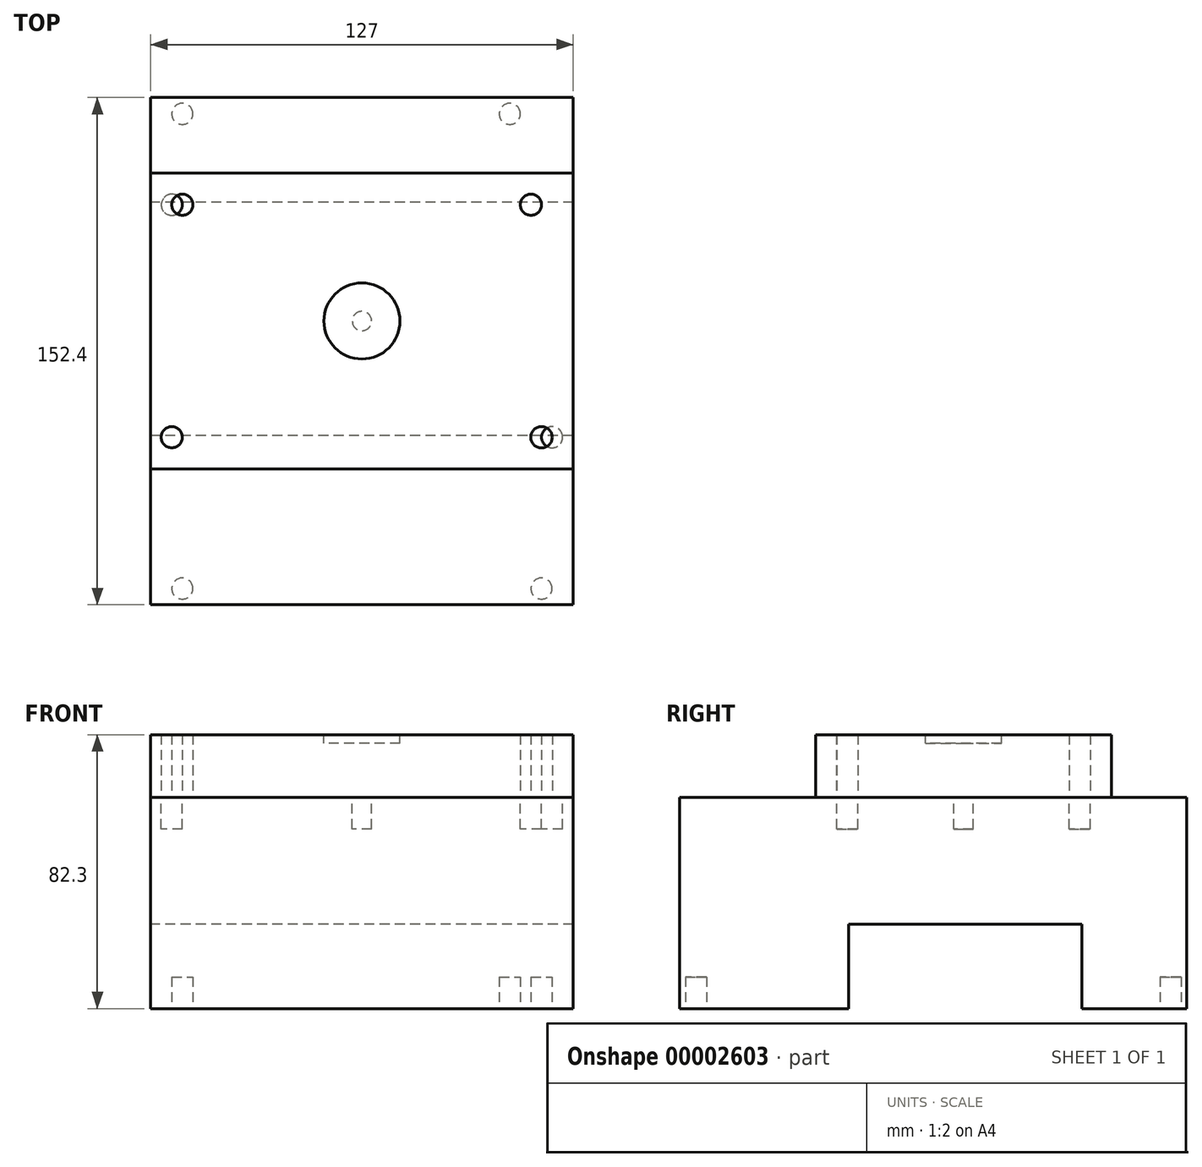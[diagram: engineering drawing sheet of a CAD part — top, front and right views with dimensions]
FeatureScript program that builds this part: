
annotation { "Feature Type Name" : "Feature", "Feature Type Description" : "" }
export const myFeature = defineFeature(function(context is Context, id is Id, definition is map)
    precondition{}
    {
        {
            var Q0;
            Q0=qCreatedBy(makeId("Top.planeOp"),FACE);
            var sketch = newSketch(context, id + "F0", { "sketchPlane" : qUnion([Q0])});
            skLineSegment(sketch, "E0.bottom", {"start": v(0, 0) * mm, "end": v(127, 0) * mm});
            skLineSegment(sketch, "E0.top", {"start": v(0, 152.4) * mm, "end": v(127, 152.4) * mm});
            skLineSegment(sketch, "E0.left", {"start": v(0, 0) * mm, "end": v(0, 152.4) * mm});
            skLineSegment(sketch, "E0.right", {"start": v(127, 0) * mm, "end": v(127, 152.4) * mm});
            skSolve(sketch);
        }
        {
            var Q0;
            Q0 = qSketchRegion(id + "F0", true);
            extrude(context, id + "F1", {"entities" : qUnion([Q0]), "depth" : 63.5 * mm});
        }
        {
            var Q0;
            Q0=makeQuery(id+"F1.opExtrude","CAP_FACE",FACE,{"disambiguationData":[OSD([sQuery(id+"F0.wireOp",EDGE,"E0.bottom"),sQuery(id+"F0.wireOp",EDGE,"E0.top"),sQuery(id+"F0.wireOp",EDGE,"E0.left"),sQuery(id+"F0.wireOp",EDGE,"E0.right")])],"isStart":true});
            var sketch = newSketch(context, id + "F2", { "sketchPlane" : qUnion([Q0])});
            skCircle(sketch, "E1", {"center": v(107.95, -147.51) * mm, "radius": 3.18 * mm});
            skCircle(sketch, "E2", {"center": v(9.52, -147.51) * mm, "radius": 3.18 * mm});
            skCircle(sketch, "E3", {"center": v(9.52, -4.89) * mm, "radius": 3.18 * mm});
            skCircle(sketch, "E4", {"center": v(117.47, -4.89) * mm, "radius": 3.18 * mm});
            skSolve(sketch);
        }
        {
            var Q0;
            Q0 = qSketchRegion(id + "F2", true);
            extrude(context, id + "F3", {"entities" : qUnion([Q0]), "operationType" : NewBodyOperationType.REMOVE, "oppositeDirection" : true, "depth" : 9.52 * mm});
        }
        {
            var Q0;
            Q0=makeQuery(id+"F1.opExtrude","CAP_FACE",FACE,{"disambiguationData":[OSD([sQuery(id+"F0.wireOp",EDGE,"E0.bottom"),sQuery(id+"F0.wireOp",EDGE,"E0.top"),sQuery(id+"F0.wireOp",EDGE,"E0.left"),sQuery(id+"F0.wireOp",EDGE,"E0.right")])],"isStart":true});
            var sketch = newSketch(context, id + "F4", { "sketchPlane" : qUnion([Q0])});
            skLineSegment(sketch, "E5.bottom", {"start": v(127, -50.8) * mm, "end": v(0, -50.8) * mm});
            skLineSegment(sketch, "E5.top", {"start": v(127, -120.9) * mm, "end": v(0, -120.9) * mm});
            skLineSegment(sketch, "E5.left", {"start": v(127, -50.8) * mm, "end": v(127, -120.9) * mm});
            skLineSegment(sketch, "E5.right", {"start": v(0, -50.8) * mm, "end": v(0, -120.9) * mm});
            skSolve(sketch);
        }
        {
            var Q0;
            Q0 = qSketchRegion(id + "F4", true);
            extrude(context, id + "F5", {"entities" : qUnion([Q0]), "operationType" : NewBodyOperationType.REMOVE, "oppositeDirection" : true, "depth" : 25.4 * mm});
        }
        {
            var Q0;
            Q0=makeQuery(id+"F1.opExtrude","CAP_FACE",FACE,{"disambiguationData":[OSD([sQuery(id+"F0.wireOp",EDGE,"E0.bottom"),sQuery(id+"F0.wireOp",EDGE,"E0.top"),sQuery(id+"F0.wireOp",EDGE,"E0.left"),sQuery(id+"F0.wireOp",EDGE,"E0.right")])],"isStart":false});
            var sketch = newSketch(context, id + "F6", { "sketchPlane" : qUnion([Q0])});
            skCircle(sketch, "E6", {"center": v(6.35, 120.2) * mm, "radius": 3.17 * mm});
            skCircle(sketch, "E7", {"center": v(114.3, 120.2) * mm, "radius": 3.17 * mm});
            skCircle(sketch, "E8", {"center": v(6.35, 50.36) * mm, "radius": 3.17 * mm});
            skCircle(sketch, "E9", {"center": v(120.65, 50.36) * mm, "radius": 3.17 * mm});
            skCircle(sketch, "E10", {"center": v(63.5, 85.28) * mm, "radius": 2.9 * mm});
            skSolve(sketch);
        }
        {
            var Q0;
            Q0 = qSketchRegion(id + "F6", true);
            extrude(context, id + "F7", {"entities" : qUnion([Q0]), "operationType" : NewBodyOperationType.REMOVE, "oppositeDirection" : true, "depth" : 9.52 * mm});
        }
        {
            var Q0;
            Q0=makeQuery(id+"F1.opExtrude","CAP_FACE",FACE,{"disambiguationData":[OSD([sQuery(id+"F0.wireOp",EDGE,"E0.bottom"),sQuery(id+"F0.wireOp",EDGE,"E0.top"),sQuery(id+"F0.wireOp",EDGE,"E0.left"),sQuery(id+"F0.wireOp",EDGE,"E0.right")])],"isStart":false});
            var sketch = newSketch(context, id + "F8", { "sketchPlane" : qUnion([Q0])});
            skLineSegment(sketch, "E11.bottom", {"start": v(0, 129.73) * mm, "end": v(127, 129.73) * mm});
            skLineSegment(sketch, "E11.top", {"start": v(0, 40.83) * mm, "end": v(127, 40.83) * mm});
            skLineSegment(sketch, "E11.left", {"start": v(0, 129.73) * mm, "end": v(0, 40.83) * mm});
            skLineSegment(sketch, "E11.right", {"start": v(127, 129.73) * mm, "end": v(127, 40.83) * mm});
            skCircle(sketch, "E12.0", {"center": v(6.35, 50.36) * mm, "radius": 3.17 * mm});
            skCircle(sketch, "E13.0", {"center": v(114.3, 120.2) * mm, "radius": 3.17 * mm});
            skLineSegment(sketch, "E14", {"start": v(6.35, 50.36) * mm, "end": v(6.35, 40.83) * mm, "construction": true});
            skLineSegment(sketch, "E15", {"start": v(114.3, 120.2) * mm, "end": v(114.3, 129.73) * mm, "construction": true});
            skCircle(sketch, "E16", {"center": v(9.52, 120.2) * mm, "radius": 3.18 * mm});
            skCircle(sketch, "E17", {"center": v(117.47, 50.36) * mm, "radius": 3.22 * mm});
            skSolve(sketch);
        }
        {
            var Q0;
            Q0 = qSketchRegion(id + "F8", true);
            extrude(context, id + "F9", {"entities" : qUnion([Q0]), "depth" : 18.8 * mm});
        }
        {
            var Q0;
            Q0=makeQuery(id+"F9.opExtrude","CAP_FACE",FACE,{"disambiguationData":[OSD([sQuery(id+"F8.wireOp",EDGE,"E11.bottom"),sQuery(id+"F8.wireOp",EDGE,"E11.top"),sQuery(id+"F8.wireOp",EDGE,"E11.left"),sQuery(id+"F8.wireOp",EDGE,"E11.right"),sQuery(id+"F8.wireOp",EDGE,"E12.0"),sQuery(id+"F8.wireOp",EDGE,"E13.0")])],"isStart":false});
            var sketch = newSketch(context, id + "F10", { "sketchPlane" : qUnion([Q0])});
            skCircle(sketch, "E18", {"center": v(63.5, 85.28) * mm, "radius": 11.43 * mm});
            skSolve(sketch);
        }
        {
            var Q0;
            Q0 = qSketchRegion(id + "F10", true);
            extrude(context, id + "F11", {"entities" : qUnion([Q0]), "operationType" : NewBodyOperationType.REMOVE, "oppositeDirection" : true, "depth" : 2.54 * mm});
        }
    });
